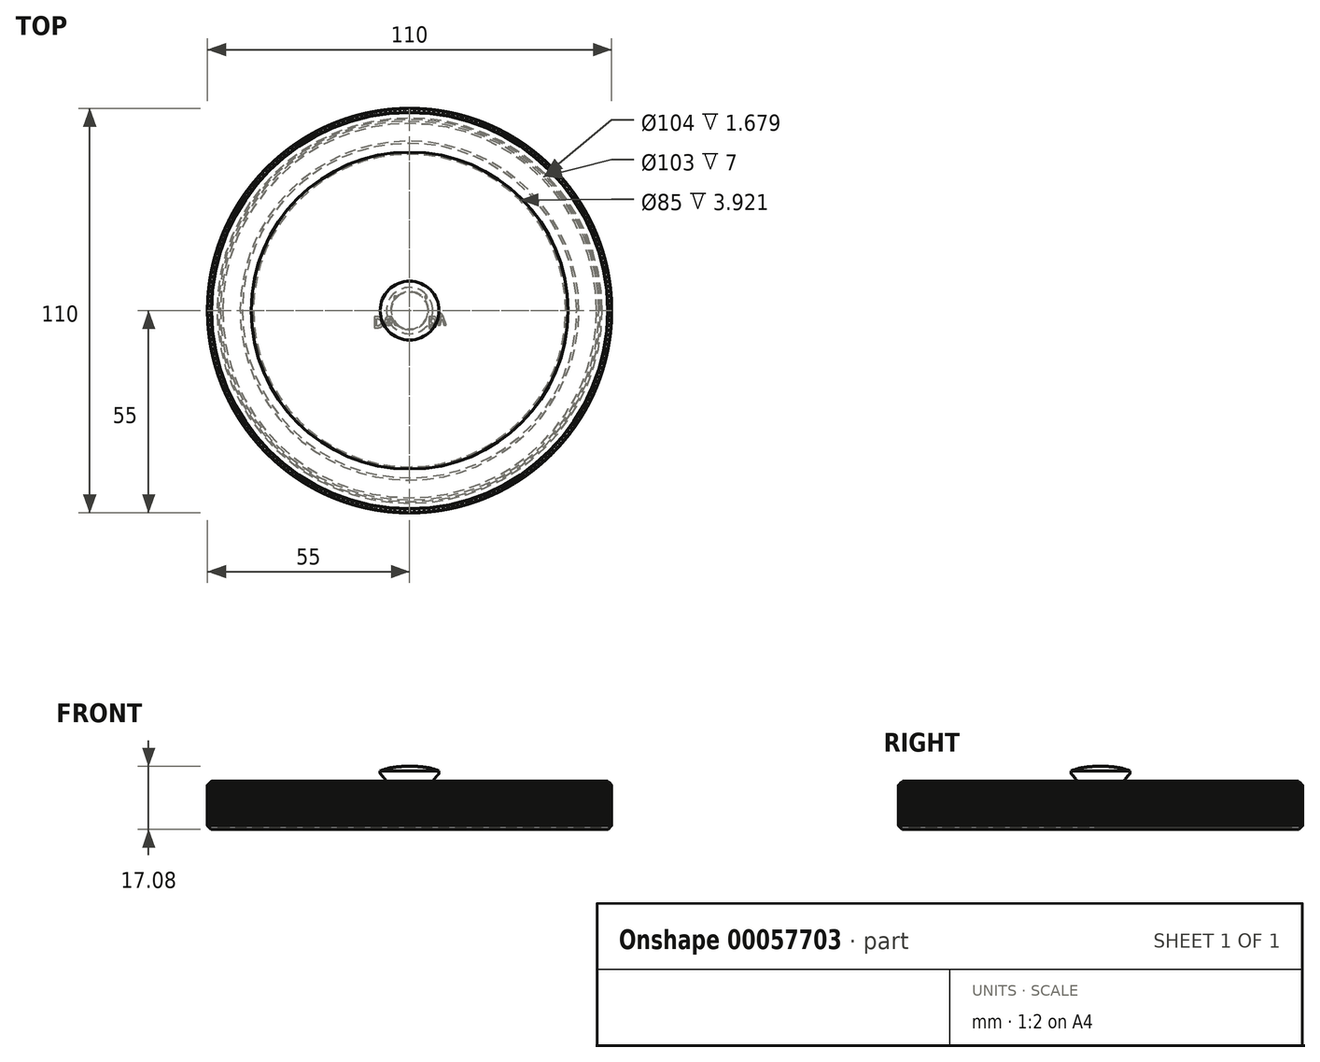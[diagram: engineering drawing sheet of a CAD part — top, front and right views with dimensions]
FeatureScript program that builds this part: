
annotation { "Feature Type Name" : "Feature", "Feature Type Description" : "" }
export const myFeature = defineFeature(function(context is Context, id is Id, definition is map)
    precondition{}
    {
        {
            var Q0;
            Q0=qCreatedBy(makeId("Front.planeOp"),FACE);
            var sketch = newSketch(context, id + "F0", { "sketchPlane" : qUnion([Q0])});
            skLineSegment(sketch, "E0", {"start": v(0, 0) * mm, "end": v(-34, 0) * mm});
            skLineSegment(sketch, "E1", {"start": v(-34, 0) * mm, "end": v(-39, 0) * mm});
            skLineSegment(sketch, "E2", {"start": v(-39, 0) * mm, "end": v(-39, -15) * mm});
            skLineSegment(sketch, "E3", {"start": v(-39, -15) * mm, "end": v(-42, -15) * mm});
            skLineSegment(sketch, "E4", {"start": v(-34.38, 1.21) * mm, "end": v(-47, 17.45) * mm});
            skLineSegment(sketch, "E5", {"start": v(-34, 0) * mm, "end": v(-34, 0.1) * mm});
            skPoint(sketch, "E6.endSnap0", {"position": v(-42, 6.13) * mm});
            skLineSegment(sketch, "E7", {"start": v(-42, 6.13) * mm, "end": v(-42, -15) * mm});
            skLineSegment(sketch, "E8", {"start": v(-50, 16.42) * mm, "end": v(-42, 6.13) * mm});
            skLineSegment(sketch, "E9", {"start": v(-46, 11.28) * mm, "end": v(-43.63, 13.12) * mm});
            skPoint(sketch, "E10.visualSharp", {"position": v(-34, 0.73) * mm});
            skArc(sketch, "E10.filletArc", {"start": v(-34, 0.1) * mm, "mid": v(-34.1, 0.7) * mm, "end": v(-34.38, 1.21) * mm});
            skLineSegment(sketch, "E11", {"start": v(-50, 76.42) * mm, "end": v(-47, 76.42) * mm});
            skLineSegment(sketch, "E12", {"start": v(-50, 76.42) * mm, "end": v(-50, 16.42) * mm});
            skLineSegment(sketch, "E13", {"start": v(-47, 76.42) * mm, "end": v(-47, 17.45) * mm});
            skLineSegment(sketch, "E14", {"start": v(-50, 83.16) * mm, "end": v(0, 83.16) * mm});
            skLineSegment(sketch, "E15", {"start": v(-42.9, 76.42) * mm, "end": v(-42.9, -15) * mm});
            skSolve(sketch);
        }
        {
            var Q0;
            Q0=qCreatedBy(makeId("Front.planeOp"),FACE);
            var sketch = newSketch(context, id + "F1", { "sketchPlane" : qUnion([Q0])});
            skLineSegment(sketch, "E16", {"start": v(0, -22.78) * mm, "end": v(0, 82.75) * mm});
            skSolve(sketch);
        }
        {
            var Q0;
            Q0=qCreatedBy(makeId("Front.planeOp"),FACE);
            var sketch = newSketch(context, id + "F2", { "sketchPlane" : qUnion([Q0])});
            skLineSegment(sketch, "E17", {"start": v(-55, 66.42) * mm, "end": v(-52, 66.42) * mm});
            skLineSegment(sketch, "E18", {"start": v(-52, 66.42) * mm, "end": v(-52, 76.42) * mm});
            skLineSegment(sketch, "E19", {"start": v(0, 79.42) * mm, "end": v(0, 76.42) * mm});
            skLineSegment(sketch, "E20", {"start": v(-52, 76.42) * mm, "end": v(-50, 76.42) * mm});
            skLineSegment(sketch, "E21", {"start": v(-55, 79.42) * mm, "end": v(-55, 66.42) * mm});
            skLineSegment(sketch, "E22", {"start": v(-55, 79.42) * mm, "end": v(0, 79.42) * mm});
            skLineSegment(sketch, "E23", {"start": v(-50, 76.42) * mm, "end": v(-47, 76.42) * mm});
            skLineSegment(sketch, "E24", {"start": v(-47, 76.42) * mm, "end": v(0, 76.42) * mm});
            skLineSegment(sketch, "E25", {"start": v(0, 79.42) * mm, "end": v(0, 0) * mm, "construction": true});
            skSolve(sketch);
        }
        {
            var Q0;
            Q0=qCreatedBy(makeId("Front.planeOp"),FACE);
            var sketch = newSketch(context, id + "F3", { "sketchPlane" : qUnion([Q0])});
            skLineSegment(sketch, "E26", {"start": v(0, 77.76) * mm, "end": v(0, 0) * mm});
            skSolve(sketch);
        }
        {
            var Q0;
            Q0 = qSketchRegion(id + "F2", true);
            var Q1;
            Q1=sQuery(id+"F3.wireOp",EDGE,"E26");
            revolve(context, id + "F4", {"entities" : qUnion([Q0]), "axis" : qUnion([Q1]), "revolveType" : RevolveType.FULL});
        }
        {
            var Q0;
            Q0=makeQuery(id+"F4.opRevolve","SWEPT_EDGE",EDGE,{"disambiguationData":[OSD([sQuery(id+"F2.wireOp",EDGE,"E21"),sQuery(id+"F2.wireOp",EDGE,"E22")])]});
            var Q1;
            Q1=makeQuery(id+"F4.opRevolve","SWEPT_EDGE",EDGE,{"disambiguationData":[OSD([sQuery(id+"F2.wireOp",EDGE,"E17"),sQuery(id+"F2.wireOp",EDGE,"E21")])]});
            chamfer(context, id + "F5", {"entities" : qUnion([Q0, Q1]), "width" : 1 * mm, "tangentPropagation" : true});
        }
        {
            var Q0;
            Q0=makeQuery(id+"F4.opRevolve","SWEPT_EDGE",EDGE,{"disambiguationData":[OSD([sQuery(id+"F2.wireOp",EDGE,"E17"),sQuery(id+"F2.wireOp",EDGE,"E18")])]});
            var Q1;
            Q1=makeQuery(id+"F4.opRevolve","SWEPT_EDGE",EDGE,{"disambiguationData":[OSD([sQuery(id+"F2.wireOp",EDGE,"hatv8aA4-DFk1-ENbV-nKXD-47W0mhsBPWlA"),sQuery(id+"F2.wireOp",EDGE,"0IibEq3d-GBF1-Pces-eTeS-5IhlWgOL7UTk")])]});
            var Q2;
            Q2=makeQuery(id+"F4.opRevolve","SWEPT_EDGE",EDGE,{"disambiguationData":[OSD([sQuery(id+"F2.wireOp",EDGE,"0IibEq3d-GBF1-Pces-eTeS-5IhlWgOL7UTk"),sQuery(id+"F2.wireOp",EDGE,"43uM3nI5-MDQ3-T33P-s8HZ-RRaWlM8MxDYb")])]});
            chamfer(context, id + "F6", {"entities" : qUnion([Q0, Q1, Q2]), "width" : 0.4 * mm, "tangentPropagation" : true});
        }
        {
            var Q0;
            Q0=qCreatedBy(makeId("Front.planeOp"),FACE);
            var sketch = newSketch(context, id + "F7", { "sketchPlane" : qUnion([Q0])});
            skLineSegment(sketch, "E27", {"start": v(-54.5, 68.5) * mm, "end": v(-51.5, 68.5) * mm});
            skLineSegment(sketch, "E28", {"start": v(-50.5, 76.5) * mm, "end": v(-46.5, 76.5) * mm});
            skLineSegment(sketch, "E29", {"start": v(-54.5, 78.5) * mm, "end": v(-54.5, 68.5) * mm});
            skLineSegment(sketch, "E30", {"start": v(-45.5, 68.5) * mm, "end": v(0, 68.5) * mm});
            skLineSegment(sketch, "E31", {"start": v(-42.5, 78.5) * mm, "end": v(-42.5, 72.5) * mm});
            skLineSegment(sketch, "E32", {"start": v(0, 71.5) * mm, "end": v(0, 68.5) * mm});
            skLineSegment(sketch, "E33", {"start": v(0, 83.5) * mm, "end": v(0, 71.5) * mm});
            skLineSegment(sketch, "E34", {"start": v(-5, 71.5) * mm, "end": v(0, 71.5) * mm});
            skLineSegment(sketch, "E35", {"start": v(-5, 72.5) * mm, "end": v(-5, 70.77) * mm});
            skLineSegment(sketch, "E36", {"start": v(-41.5, 71.5) * mm, "end": v(-6, 71.5) * mm});
            skPoint(sketch, "E37.visualSharp", {"position": v(-8, 81.5) * mm});
            skPoint(sketch, "E38.visualSharp", {"position": v(-5, 71.5) * mm});
            skArc(sketch, "E38.filletArc", {"start": v(-6, 71.5) * mm, "mid": v(-5.3, 71.8) * mm, "end": v(-5, 72.5) * mm});
            skPoint(sketch, "E39.visualSharp", {"position": v(-42.5, 71.5) * mm});
            skArc(sketch, "E39.filletArc", {"start": v(-42.5, 72.5) * mm, "mid": v(-42.2, 71.8) * mm, "end": v(-41.5, 71.5) * mm});
            skLineSegment(sketch, "E40", {"start": v(0, 83.5) * mm, "end": v(-1.5, 83.5) * mm});
            skLineSegment(sketch, "E41", {"start": v(-53.5, 79.5) * mm, "end": v(-43.5, 79.5) * mm});
            skPoint(sketch, "E42.visualSharp", {"position": v(-54.5, 79.5) * mm});
            skArc(sketch, "E42.filletArc", {"start": v(-53.5, 79.5) * mm, "mid": v(-54.2, 79.2) * mm, "end": v(-54.5, 78.5) * mm});
            skPoint(sketch, "E43.visualSharp", {"position": v(-42.5, 79.5) * mm});
            skArc(sketch, "E43.filletArc", {"start": v(-42.5, 78.5) * mm, "mid": v(-42.8, 79.2) * mm, "end": v(-43.5, 79.5) * mm});
            skLineSegment(sketch, "E44", {"start": v(0, 0) * mm, "end": v(0, 68.5) * mm});
            skLineSegment(sketch, "E45", {"start": v(-7.59, 81.08) * mm, "end": v(-7.77, 81.27) * mm});
            skLineSegment(sketch, "E46", {"start": v(-5, 72.5) * mm, "end": v(-5, 74.77) * mm});
            skLineSegment(sketch, "E47", {"start": v(-8, 82.3) * mm, "end": v(-8, 81.83) * mm});
            skPoint(sketch, "E48.visualSharp", {"position": v(-5, 78.46) * mm});
            skArc(sketch, "E48.filletArc", {"start": v(-5, 74.77) * mm, "mid": v(-5.67, 78.18) * mm, "end": v(-7.59, 81.08) * mm});
            skArc(sketch, "E49.filletArc", {"start": v(-8, 81.83) * mm, "mid": v(-7.94, 81.52) * mm, "end": v(-7.77, 81.27) * mm});
            skArc(sketch, "E50", {"start": v(-1.5, 83.5) * mm, "mid": v(-4.8, 83.2) * mm, "end": v(-8, 82.3) * mm});
            skLineSegment(sketch, "E51", {"start": v(0, 84.48) * mm, "end": v(-8, 84.48) * mm});
            skLineSegment(sketch, "E52", {"start": v(-51.5, 68.5) * mm, "end": v(-51.5, 75.5) * mm});
            skLineSegment(sketch, "E53", {"start": v(-45.5, 68.5) * mm, "end": v(-45.5, 75.5) * mm});
            skPoint(sketch, "E54.visualSharp", {"position": v(-51.5, 76.5) * mm});
            skArc(sketch, "E54.filletArc", {"start": v(-50.5, 76.5) * mm, "mid": v(-51.2, 76.2) * mm, "end": v(-51.5, 75.5) * mm});
            skPoint(sketch, "E55.visualSharp", {"position": v(-45.5, 76.5) * mm});
            skArc(sketch, "E55.filletArc", {"start": v(-45.5, 75.5) * mm, "mid": v(-45.8, 76.2) * mm, "end": v(-46.5, 76.5) * mm});
            skSolve(sketch);
        }
        {
            var Q0;
            Q0 = qSketchRegion(id + "F7", true);
            var Q1;
            Q1=sQuery(id+"F3.wireOp",EDGE,"E26");
            revolve(context, id + "F8", {"entities" : qUnion([Q0]), "axis" : qUnion([Q1]), "revolveType" : RevolveType.FULL});
        }
        {
            var Q0;
            Q0=makeQuery(id+"F4.opRevolve","SWEPT_FACE",FACE,{"disambiguationData":[OSD([sQuery(id+"F2.wireOp",EDGE,"E22")])]});
            var sketch = newSketch(context, id + "F9", { "sketchPlane" : qUnion([Q0])});
            skLineSegment(sketch, "E56", {"start": v(-0.5, 55) * mm, "end": v(0, 54.5) * mm});
            skLineSegment(sketch, "E57", {"start": v(0, 54.5) * mm, "end": v(0.5, 55) * mm});
            skLineSegment(sketch, "E58", {"start": v(0, 54.5) * mm, "end": v(0, 54.5) * mm, "construction": true});
            skLineSegment(sketch, "E59", {"start": v(-0.5, 55) * mm, "end": v(0.5, 55) * mm});
            skSolve(sketch);
        }
        {
            var Q0;
            Q0=makeQuery(id+"F9.imprint","IMPRINT",FACE,{"disambiguationData":[TD([[makeQuery(id+"F9.imprint","IMPRINT",EDGE,{"derivedFrom":sQuery(id+"F9.wireOp",EDGE,"E56")}),1.0]])]});
            extrude(context, id + "F10", {"entities" : qUnion([Q0]), "oppositeDirection" : true, "depth" : 12 * mm});
        }
        {
            var Q0;
            Q0=makeQuery(id+"F10.opExtrude","SWEPT_BODY",BODY,{"disambiguationData":[OSD([sQuery(id+"F9.wireOp",EDGE,"379RDas3-0WoG-w0gh-eJQp-VD7GTOvTa7Rq"),sQuery(id+"F9.wireOp",EDGE,"216987a8-6be4-4b1f-9b76-40902a50daca0.MirrorCS"),sQuery(id+"F9.wireOp",EDGE,"E56"),sQuery(id+"F9.wireOp",EDGE,"E57")])]});
            var Q1;
            Q1=sQuery(id+"F1.wireOp",EDGE,"E16");
            circularPattern(context, id + "F11", {"operationType" : NewBodyOperationType.REMOVE, "entities" : qUnion([Q0]), "axis" : qUnion([Q1]), "angle" : 360 * degree, "instanceCount" : 260, "equalSpace" : true});
        }
        {
            var Q0;
            Q0=makeQuery(id+"F4.opRevolve","SWEPT_FACE",FACE,{"disambiguationData":[OSD([sQuery(id+"F2.wireOp",EDGE,"E20"),sQuery(id+"F2.wireOp",EDGE,"E23"),sQuery(id+"F2.wireOp",EDGE,"E24")])]});
            var sketch = newSketch(context, id + "F12", { "sketchPlane" : qUnion([Q0])});
            skText(sketch, "E60", { "text": "Design by\n     M. S. ", "fontName": "OpenSans-Bold.ttf"});
            const initialGuessF12  = {"E60": [-0.01, 0.00169, 1, 0, 0.00299]};
            skSetInitialGuess(sketch, initialGuessF12);
            skSolve(sketch);
        }
        {
            var Q0;
            Q0 = qSketchRegion(id + "F12", true);
            extrude(context, id + "F13", {"entities" : qUnion([Q0]), "operationType" : NewBodyOperationType.ADD, "depth" : 0.5 * mm});
        }
    });
